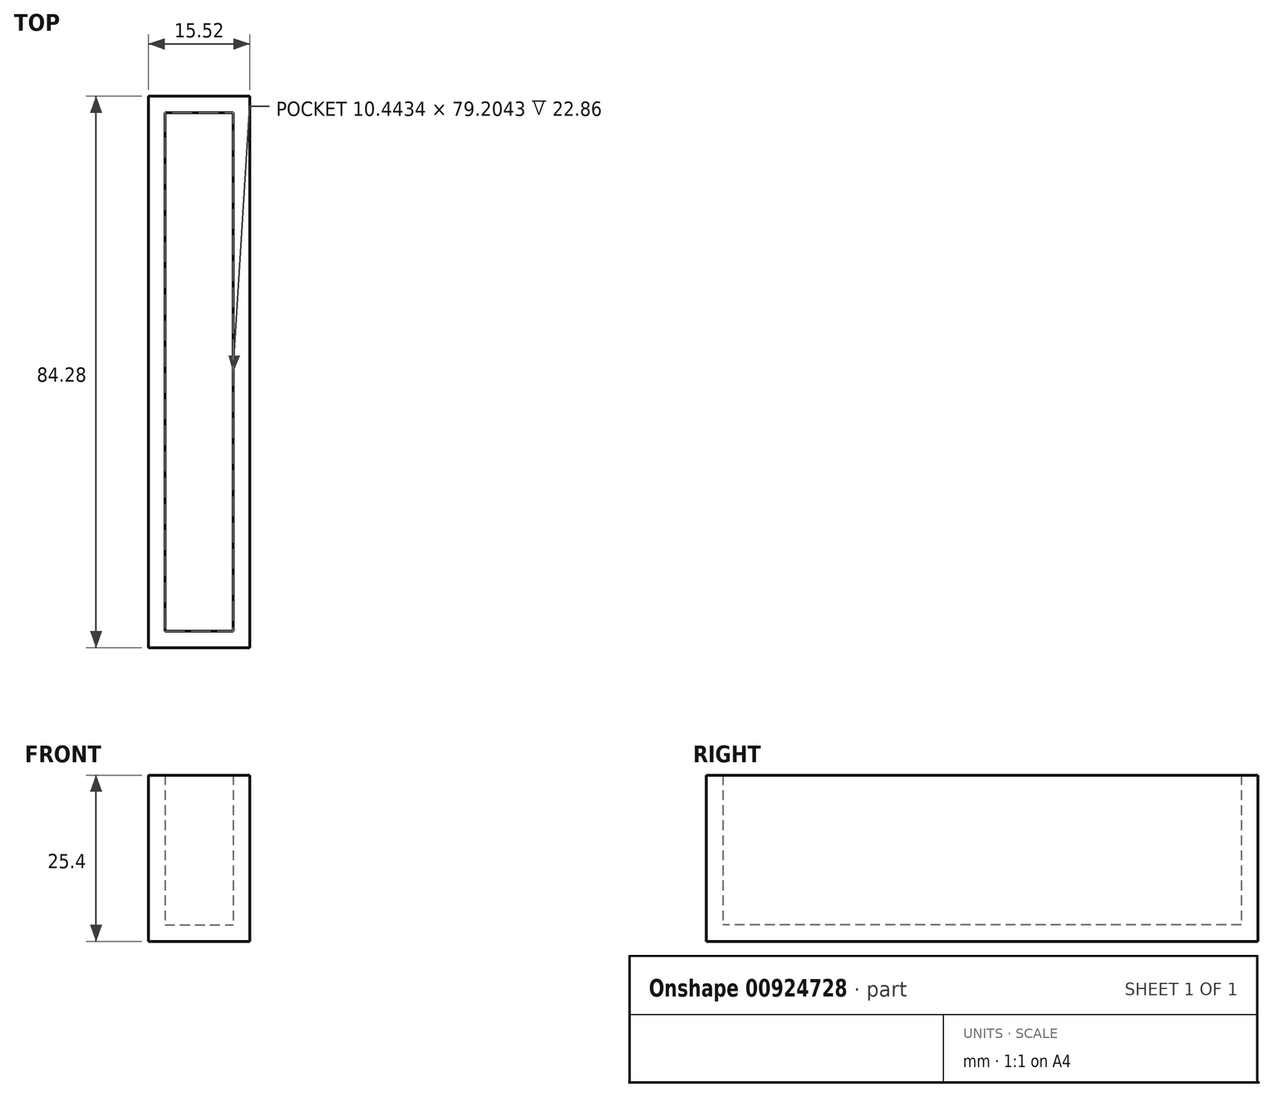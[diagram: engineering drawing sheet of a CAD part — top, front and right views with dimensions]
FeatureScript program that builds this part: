
annotation { "Feature Type Name" : "Feature", "Feature Type Description" : "" }
export const myFeature = defineFeature(function(context is Context, id is Id, definition is map)
    precondition{}
    {
        {
            var Q0;
            Q0=qCreatedBy(makeId("Top.planeOp"),FACE);
            var sketch = newSketch(context, id + "F0", { "sketchPlane" : qUnion([Q0])});
            skLineSegment(sketch, "E0.bottom", {"start": v(-16.94, 41.97) * mm, "end": v(-1.42, 41.97) * mm});
            skLineSegment(sketch, "E0.top", {"start": v(-16.94, -42.31) * mm, "end": v(-1.42, -42.31) * mm});
            skLineSegment(sketch, "E0.left", {"start": v(-16.94, 41.97) * mm, "end": v(-16.94, -42.31) * mm});
            skLineSegment(sketch, "E0.right", {"start": v(-1.42, 41.97) * mm, "end": v(-1.42, -42.31) * mm});
            skArc(sketch, "E1", {"start": v(-7.81, 52.77) * mm, "mid": v(-24.01, 57.2) * mm, "end": v(-16.94, 41.97) * mm});
            skSolve(sketch);
        }
        {
            var Q0;
            Q0 = qSketchRegion(id + "F0", true);
            extrude(context, id + "F1", {"entities" : qUnion([Q0]), "depth" : 25.4 * mm, "offsetDistance" : 25.4 * mm});
        }
        {
            var Q0;
            Q0=makeQuery(id+"F1.opExtrude","CAP_FACE",FACE,{"disambiguationData":[OSD([sQuery(id+"F0.wireOp",EDGE,"E0.bottom"),sQuery(id+"F0.wireOp",EDGE,"E0.top"),sQuery(id+"F0.wireOp",EDGE,"E0.left"),sQuery(id+"F0.wireOp",EDGE,"E0.right")])],"isStart":false});
            shell(context, id + "F2", {"entities" : qUnion([Q0]), "thickness" : 2.54 * mm});
        }
    });
